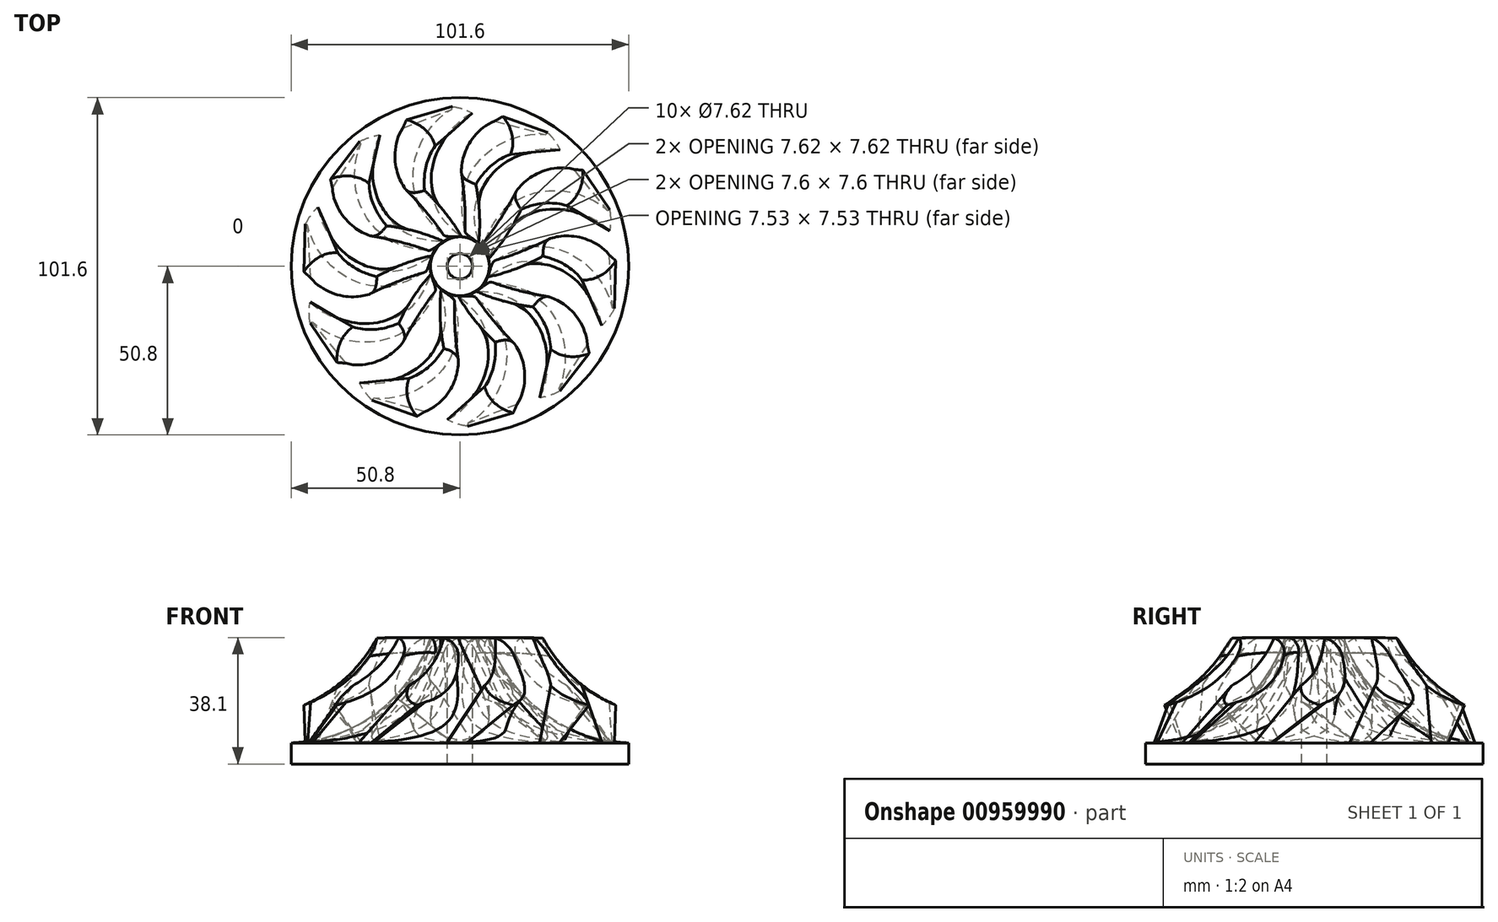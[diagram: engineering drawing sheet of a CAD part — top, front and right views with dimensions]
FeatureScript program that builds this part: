
annotation { "Feature Type Name" : "Feature", "Feature Type Description" : "" }
export const myFeature = defineFeature(function(context is Context, id is Id, definition is map)
    precondition{}
    {
        {
            var Q0;
            Q0=qCreatedBy(makeId("Front.planeOp"),FACE);
            var sketch = newSketch(context, id + "F0", { "sketchPlane" : qUnion([Q0])});
            skLineSegment(sketch, "E0", {"start": v(0, 0) * mm, "end": v(50.8, 0) * mm});
            skLineSegment(sketch, "E1", {"start": v(50.8, 0) * mm, "end": v(50.8, 6.35) * mm});
            skLineSegment(sketch, "E2", {"start": v(0, 0) * mm, "end": v(0, 38.1) * mm});
            skLineSegment(sketch, "E3", {"start": v(0, 38.1) * mm, "end": v(8.9, 38.1) * mm});
            skArc(sketch, "E4", {"start": v(8.9, 38.1) * mm, "mid": v(24.82, 15.6) * mm, "end": v(50.8, 6.35) * mm});
            skSolve(sketch);
        }
        {
            var Q0;
            Q0=makeQuery(id+"F0.imprint","IMPRINT",FACE,{"disambiguationData":[TD([[makeQuery(id+"F0.imprint","IMPRINT",EDGE,{"derivedFrom":sQuery(id+"F0.wireOp",EDGE,"E0")}),1.0]])]});
            var Q1;
            Q1=sQuery(id+"F0.wireOp",EDGE,"E2");
            revolve(context, id + "F1", {"surfaceOperationType" : NewSurfaceOperationType.NEW, "entities" : qUnion([Q0]), "axis" : qUnion([Q1]), "revolveType" : RevolveType.FULL});
        }
        {
            var Q0;
            Q0=makeQuery(id+"F1.opRevolve","SWEPT_FACE",FACE,{"disambiguationData":[OSD([sQuery(id+"F0.wireOp",EDGE,"E0")])]});
            var sketch = newSketch(context, id + "F2", { "sketchPlane" : qUnion([Q0])});
            skArc(sketch, "E5", {"start": v(0, 0) * mm, "mid": v(9.76, 27.34) * mm, "end": v(-8.22, 50.13) * mm});
            skArc(sketch, "E6", {"start": v(1.52, 0) * mm, "mid": v(11.55, 27.2) * mm, "end": v(-5.7, 50.48) * mm});
            skLineSegment(sketch, "E7", {"start": v(1.52, 0) * mm, "end": v(0, 0) * mm});
            skArc(sketch, "E8", {"start": v(-5.7, 50.48) * mm, "mid": v(-6.96, 50.3) * mm, "end": v(-8.22, 50.13) * mm});
            skSolve(sketch);
        }
        {
            var Q0;
            Q0=makeQuery(id+"F1.opRevolve","SWEPT_FACE",FACE,{"disambiguationData":[OSD([sQuery(id+"F0.wireOp",EDGE,"E3")])]});
            var sketch = newSketch(context, id + "F3", { "sketchPlane" : qUnion([Q0])});
            skArc(sketch, "E9", {"start": v(0, 0) * mm, "mid": v(15.8, -22.22) * mm, "end": v(41.16, -32.26) * mm});
            skArc(sketch, "E10", {"start": v(-4.63, 0) * mm, "mid": v(13.1, -24.85) * mm, "end": v(41.16, -36.87) * mm});
            skLineSegment(sketch, "E11", {"start": v(41.16, -36.87) * mm, "end": v(41.16, -32.26) * mm});
            skLineSegment(sketch, "E12", {"start": v(-4.63, 0) * mm, "end": v(0, 0) * mm});
            skSolve(sketch);
        }
        {
            var Q1;
            {var subQ0=sQuery(id+"F3.wireOp",EDGE,"E11");Q1=makeQuery(id+"F3.imprint","IMPRINT",FACE,{"disambiguationData":[TD([[makeQuery(id+"F3.imprint","IMPRINT",EDGE,{"derivedFrom":subQ0}),1.0]])]});}
            var Q2;
            Q2=makeQuery(id+"F2.imprint","IMPRINT",FACE,{"disambiguationData":[TD([[makeQuery(id+"F2.imprint","IMPRINT",EDGE,{"derivedFrom":sQuery(id+"F2.wireOp",EDGE,"E5")}),-1.0]])]});
            loft(context, id + "F4", {"operationType" : NewBodyOperationType.ADD, "sheetProfilesArray" : [{ "sheetProfileEntities" : qUnion([Q1]) }, { "sheetProfileEntities" : qUnion([Q2]) }]});
        }
        {
            var Q0;
            Q0=qCreatedBy(makeId("Front.planeOp"),FACE);
            var sketch = newSketch(context, id + "F5", { "sketchPlane" : qUnion([Q0])});
            skLineSegment(sketch, "E13", {"start": v(0, 0) * mm, "end": v(-50.8, 0) * mm});
            skLineSegment(sketch, "E14", {"start": v(-50.8, 0) * mm, "end": v(-50.8, 16.32) * mm});
            skLineSegment(sketch, "E15", {"start": v(0, 0) * mm, "end": v(0, -13.83) * mm});
            skLineSegment(sketch, "E16", {"start": v(0, -13.83) * mm, "end": v(-66.48, -13.83) * mm});
            skLineSegment(sketch, "E17", {"start": v(-66.48, -13.83) * mm, "end": v(-66.48, 40.67) * mm});
            skLineSegment(sketch, "E18", {"start": v(-66.48, 40.67) * mm, "end": v(-23.9, 40.67) * mm});
            skArc(sketch, "E19", {"start": v(-50.8, 16.32) * mm, "mid": v(-34.7, 25.57) * mm, "end": v(-23.9, 40.67) * mm});
            skSolve(sketch);
        }
        {
            var Q0;
            Q0=makeQuery(id+"F5.imprint","IMPRINT",FACE,{"disambiguationData":[TD([[makeQuery(id+"F5.imprint","IMPRINT",EDGE,{"derivedFrom":sQuery(id+"F5.wireOp",EDGE,"E13")}),1.0]])]});
            var Q1;
            Q1=sQuery(id+"F5.wireOp",EDGE,"E15");
            revolve(context, id + "F6", {"operationType" : NewBodyOperationType.REMOVE, "surfaceOperationType" : NewSurfaceOperationType.NEW, "entities" : qUnion([Q0]), "axis" : qUnion([Q1]), "revolveType" : RevolveType.FULL, "oppositeDirection" : true});
        }
        {
            var Q0;
            Q0=makeQuery(id+"F4.opLoft","MID_CAP_EDGE",EDGE,{"disambiguationData":[OSD([sQuery(id+"F0.wireOp",EDGE,"E3"),sQuery(id+"F0.wireOp",EDGE,"E4"),sQuery(id+"F3.wireOp",EDGE,"E9"),sQuery(id+"F3.wireOp",EDGE,"E11")])],"capPos":0.0});
            fillet(context, id + "F7", {"entities" : qUnion([Q0]), "radius" : 5.08 * mm, "tangentPropagation" : true, "allowEdgeOverflow" : false});
        }
        {
            var Q0;
            {var subQ0=sQuery(id+"F3.wireOp",EDGE,"E11");var subQ2=sQuery(id+"F0.wireOp",EDGE,"E3");Q0=makeQuery(id+"F4.boolean.opBoolean","MERGE",FACE,{"derivedFrom":[makeQuery(id+"F1.opRevolve","SWEPT_FACE",FACE,{"disambiguationData":[OSD([subQ2])]}),makeQuery(id+"F4.opLoft","CAP_FACE",FACE,{"disambiguationData":[OSD([makeQuery(id+"F3.imprint","IMPRINT",FACE,{"disambiguationData":[TD([[makeQuery(id+"F3.imprint","IMPRINT",EDGE,{"derivedFrom":subQ0}),1.0]])]})])],"isStart":true})]});}
            var sketch = newSketch(context, id + "F8", { "sketchPlane" : qUnion([Q0])});
            skCircle(sketch, "E20", {"center": v(0, 0) * mm, "radius": 3.81 * mm});
            skSolve(sketch);
        }
        {
            var Q0;
            Q0=makeQuery(id+"F8.imprint","IMPRINT",FACE,{"disambiguationData":[TD([[makeQuery(id+"F8.imprint","IMPRINT",EDGE,{"derivedFrom":sQuery(id+"F8.wireOp",EDGE,"E20")}),1.0]])]});
            extrude(context, id + "F9", {"entities" : qUnion([Q0]), "operationType" : NewBodyOperationType.REMOVE, "endBound" : BoundingType.THROUGH_ALL, "oppositeDirection" : true, "depth" : 25.4 * mm, "offsetDistance" : 25.4 * mm});
        }
        {
            var Q0;
            {var subQ0=sQuery(id+"F3.wireOp",EDGE,"E11");var subQ2=sQuery(id+"F0.wireOp",EDGE,"E3");Q0=makeQuery(id+"F4.boolean.opBoolean","MERGE",FACE,{"derivedFrom":[makeQuery(id+"F1.opRevolve","SWEPT_FACE",FACE,{"disambiguationData":[OSD([subQ2])]}),makeQuery(id+"F4.opLoft","CAP_FACE",FACE,{"disambiguationData":[OSD([makeQuery(id+"F3.imprint","IMPRINT",FACE,{"disambiguationData":[TD([[makeQuery(id+"F3.imprint","IMPRINT",EDGE,{"derivedFrom":subQ0}),1.0]])]})])],"isStart":true})]});}
            var sketch = newSketch(context, id + "F10", { "sketchPlane" : qUnion([Q0])});
            skPoint(sketch, "E21", {"position": v(0, 0) * mm});
            skPoint(sketch, "E22", {"position": v(8.9, 0) * mm});
            skSolve(sketch);
        }
        {
            var Q0;
            Q0=makeQuery(id+"F1.opRevolve","SWEPT_FACE",FACE,{"disambiguationData":[OSD([sQuery(id+"F0.wireOp",EDGE,"E0")])]});
            var sketch = newSketch(context, id + "F11", { "sketchPlane" : qUnion([Q0])});
            skPoint(sketch, "E23", {"position": v(0, 0) * mm});
            skSolve(sketch);
        }
        {
            var Q0;
            Q0=sQuery(id+"F10.wireOp",VERTEX,"E21");
            var Q1;
            Q1=sQuery(id+"F10.wireOp",VERTEX,"E22");
            var Q2;
            Q2=sQuery(id+"F11.wireOp",VERTEX,"E23");
            cPlane(context, id + "F12", {"entities" : qUnion([Q0, Q1, Q2]), "cplaneType" : CPlaneType.THREE_POINT, "offset" : 25.4 * mm, "width" : 152.4 * mm, "height" : 152.4 * mm});
        }
        {
            var Q0;
            Q0=qCreatedBy(id+"F12.planeOp",FACE);
            var sketch = newSketch(context, id + "F13", { "sketchPlane" : qUnion([Q0])});
            skLineSegment(sketch, "E24", {"start": v(0, 38.55) * mm, "end": v(0, 0) * mm, "construction": true});
            skSolve(sketch);
        }
        {
            var Q0;
            Q0=makeQuery(id+"F1.opRevolve","SWEPT_BODY",BODY,{"disambiguationData":[OSD([sQuery(id+"F0.wireOp",EDGE,"E0"),sQuery(id+"F0.wireOp",EDGE,"E1"),sQuery(id+"F0.wireOp",EDGE,"E2"),sQuery(id+"F0.wireOp",EDGE,"E3"),sQuery(id+"F0.wireOp",EDGE,"E4")])]});
            var Q1;
            Q1=sQuery(id+"F13.wireOp",EDGE,"E24");
            circularPattern(context, id + "F14", {"entities" : qUnion([Q0]), "axis" : qUnion([Q1]), "angle" : 360 * degree, "instanceCount" : 10, "equalSpace" : true});
        }
    });
